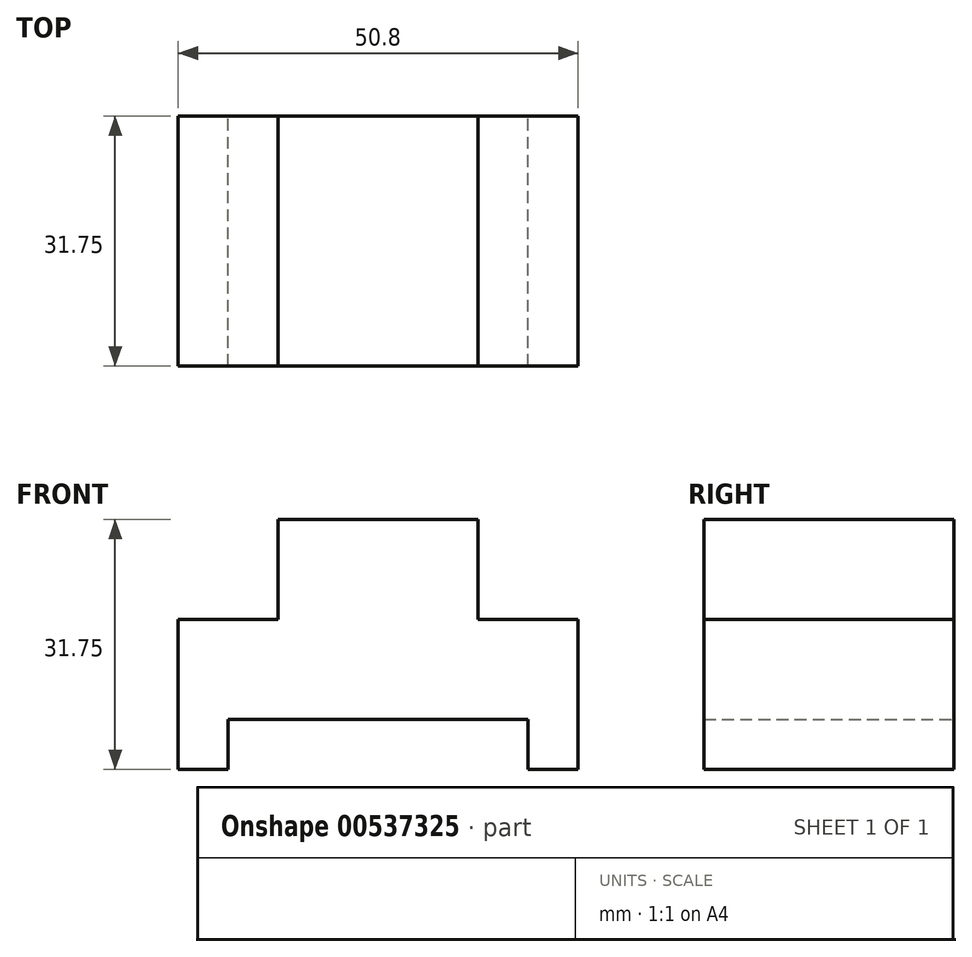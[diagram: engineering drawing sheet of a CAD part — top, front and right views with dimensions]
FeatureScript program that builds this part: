
annotation { "Feature Type Name" : "Feature", "Feature Type Description" : "" }
export const myFeature = defineFeature(function(context is Context, id is Id, definition is map)
    precondition{}
    {
        {
            var Q0;
            Q0=qCreatedBy(makeId("Front.planeOp"),FACE);
            var sketch = newSketch(context, id + "F0", { "sketchPlane" : qUnion([Q0])});
            skLineSegment(sketch, "E0", {"start": v(-41.2, 0) * mm, "end": v(-34.84, 0) * mm});
            skLineSegment(sketch, "E1", {"start": v(-34.84, 0) * mm, "end": v(-34.84, 6.35) * mm});
            skLineSegment(sketch, "E2", {"start": v(-34.84, 6.35) * mm, "end": v(3.26, 6.35) * mm});
            skLineSegment(sketch, "E3", {"start": v(3.26, 6.35) * mm, "end": v(3.26, 0) * mm});
            skLineSegment(sketch, "E4", {"start": v(3.26, 0) * mm, "end": v(9.6, 0) * mm});
            skLineSegment(sketch, "E5", {"start": v(9.6, 0) * mm, "end": v(9.6, 19.05) * mm});
            skLineSegment(sketch, "E6", {"start": v(9.6, 19.05) * mm, "end": v(-3.1, 19.05) * mm});
            skLineSegment(sketch, "E7", {"start": v(-3.1, 19.05) * mm, "end": v(-3.1, 31.75) * mm});
            skLineSegment(sketch, "E8", {"start": v(-3.1, 31.75) * mm, "end": v(-28.5, 31.75) * mm});
            skLineSegment(sketch, "E9", {"start": v(-28.5, 31.75) * mm, "end": v(-28.5, 19.05) * mm});
            skLineSegment(sketch, "E10", {"start": v(-28.5, 19.05) * mm, "end": v(-41.2, 19.05) * mm});
            skLineSegment(sketch, "E11", {"start": v(-41.2, 19.05) * mm, "end": v(-41.2, 0) * mm});
            skSolve(sketch);
        }
        {
            var Q0;
            Q0=makeQuery(id+"F0.imprint","IMPRINT",FACE,{"disambiguationData":[TD([[makeQuery(id+"F0.imprint","IMPRINT",EDGE,{"derivedFrom":sQuery(id+"F0.wireOp",EDGE,"E0")}),1.0]])]});
            extrude(context, id + "F1", {"entities" : qUnion([Q0]), "depth" : 31.75 * mm, "offsetDistance" : 25.4 * mm});
        }
    });
